# Revit family: 24QBR.QBR-B_231217_2
name_source: partatom
category: 통신 장치
units: mm (PartAtom-declared; Revit-internal decimal feet)

## family parameters
OmniClass 번호 = 23.85.10.14.24
OmniClass 제목 = Video Monitors
공유 = 아니오
로드될 때 보이드를 사용하여 절단 = 아니오
룸 계산 점 = 아니오
부품 유형 = 보통
원형 커넥터 치수 = 지름 사용
작업 기준면 기반 = 아니오
주석 방향을 유지합니다. = 아니오
항상 수직 = 예

## types (2) — shared parameters
Active Display Area = 527.04 (H) x 296.46 (V)
Bezel Width L/R (mm) = 9.4  [stored 0.0308399 ft]
Bezel Width U/B (mm) = 17.9
Brightness (Typ.) = 250
Color Gamut = 72%
Contrast Ratio (Typ.) = 1000:1
Diagonal Size (Class) = 24  [stored 0.0787402 ft]
Diagonal Size (Measured) = 23.8
Dimension Package (mm) = 620 x 419 x 122
Dimension Set (mm) = 547.9 x 334.4 x 31.8
Dimension Set Depth (mm) = 31.8  [stored 0.104331 ft]
Dimension Set Height (mm) = 334.4  [stored 1.09711 ft]
Dimension Set Width (mm) = 547.9  [stored 1.79757 ft]
Display Colors = 16.7 M (real 6bit, dither 8bit)
Dynamic C/R = MEGA
EMC = Class B
Environment = ENERGY STAR 8.0, EPEAT
External Control = RS232C(in/out) thru stereo jack, RJ45
H-Scanning Frequency = 56 ~ 84.5kHz
Haze = 25%
Input HDCP = HDCP2.2
Input RGB = -
Input USB = USB 2.0 x 1
Input Video = HDMI 1.4 (1)
Internal Clock Speed = 1.7GHz
Internal Graphics = Graphic resolution : 1920x1080 Output resolution : 1920x1080 (Scale up from graphic processing result.)
Internal IO Ports = USB 2.0
Internal Main Memory Interface = 2.5GB, LPDDR4 1.5GHz 64bit
Internal Multimedia = Video Decoder  : MPEG-1/2/4, H.263, H.264/AVC, UHD H.264/AVC,  VC-1, HEVC, JPEG, PNG, VP8, VP9  *Audio Decoder : AC3 (DD), MPEG
Internal On-Chip Cache Memory = L1 Instruction Cache : 48KB L1 Data Cache : 32KB L2 Cache : 2MB
Internal Operating System = Tizen 4.0 (VDLinux)
Internal Processor = Cortex A72 1.7GHz Quad-Core CPU
Internal Storage (FDM) = 8GB (3.88GB Occupied by O/S, 4.12GB Available)
Key = Small Signage Display Slim & Light Signage with Built-in MagicInfo S6, SSSP 6.0
Maximum Pixel Frequency = 594MHz
Operation Hour = 16/7
Optional Mount = -
Optional Specialty = -
Optional Stand = -
Orientation = Landscape / Portrait
Output Audio = Stereo mini Jack
Pixel Pitch (mm) = 0.2745 x 0.2745
Power Consumption BTU(Max) = 131.3
Power Consumption Max [W/h] = 38.5
Power Consumption Rating [W/h] = 35
Power Consumption Sleep mode = 0.5
Power Consumption Typical [W/h] = 25
Power Supply = AC100 - 240V, 50/60 Hz
Power Type = Internal
Relative Humidity = 10~80%
Resolution = FHD (1920 x 1080)
Response Time (GtoG) = 14ms
Safety = 60950-1
Screen = Samsung Electornics Screen
Security = 802.1 x (WPA2 Enterprise) : EAP-TLS, EAP-TTLS, EAP-PEAP
Sound = Built in Speaker(5W)
Temperature = 0℃ ~ 40℃
Type = ADS
V-Scanning Frequency = 48 ~ 75HZ
VESA Mount = 100 x 100
Viewing Angle(H/V) = 178/178
Weight Package (kg) = 4.1
Weight Set (kg) = 3
제조업체 = Samsung Electronics Co., Ltd.
조합 코드 = E1020500
키노트 = 11 52 00

## per-type parameters (varying)
| type | 모델 |
| Small Signage QB24R | UHD Signage QB24R |
| Small Signage QB24R-B | UHD Signage QB24R-B |

note: [stored X ft] marks values corroborated as IEEE doubles in the binary element streams (Revit-internal decimal feet)
